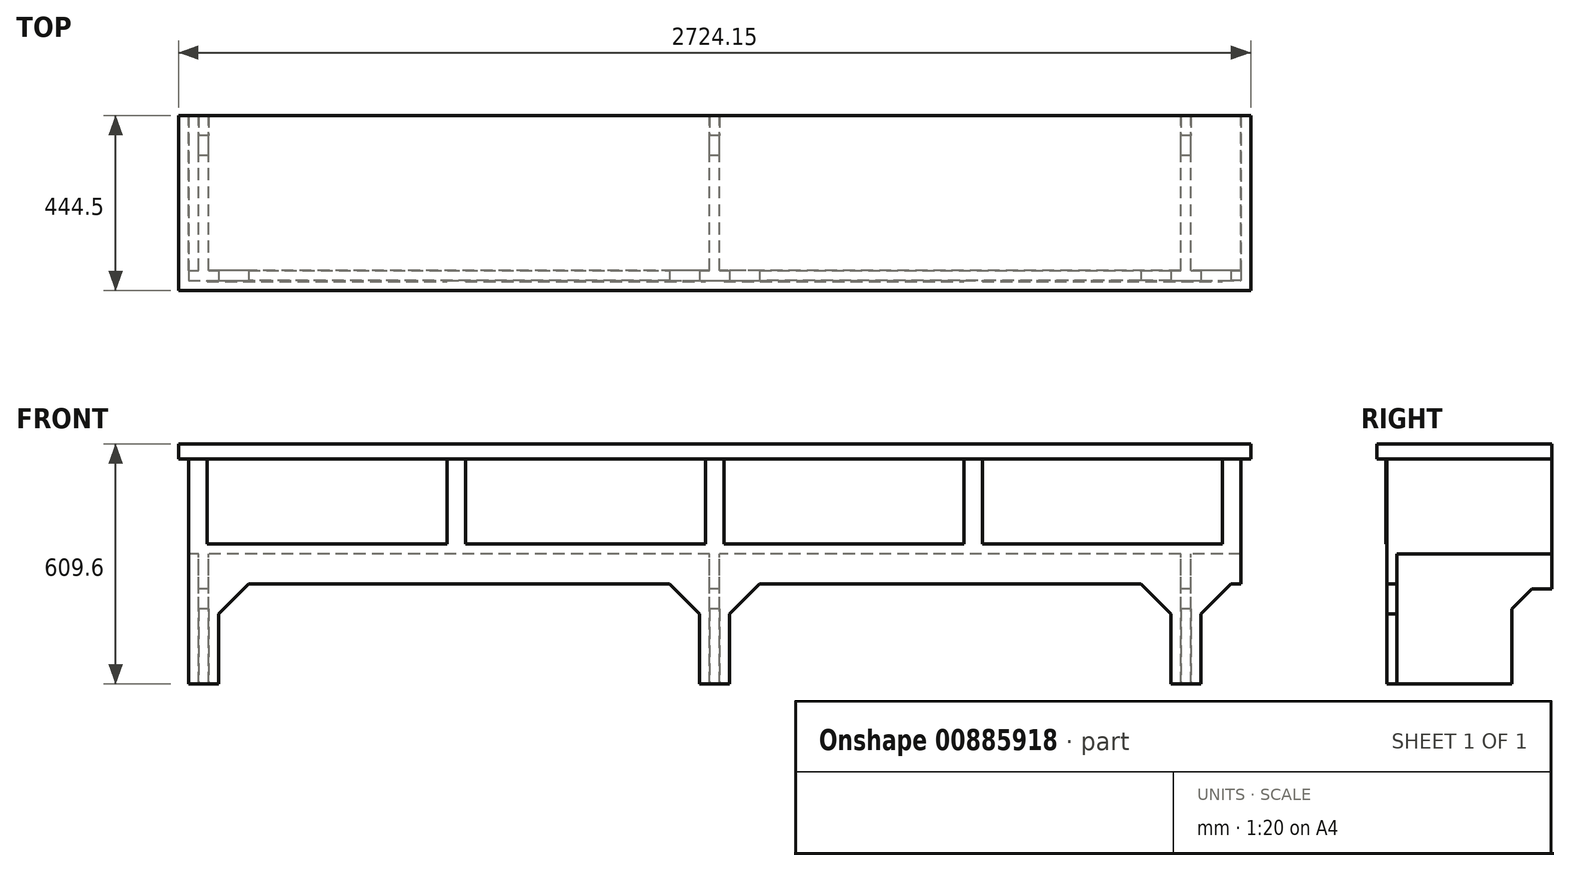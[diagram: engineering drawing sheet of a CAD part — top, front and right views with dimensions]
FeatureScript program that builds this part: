
annotation { "Feature Type Name" : "Feature", "Feature Type Description" : "" }
export const myFeature = defineFeature(function(context is Context, id is Id, definition is map)
    precondition{}
    {
        {
            var Q0;
            Q0=qCreatedBy(makeId("Top.planeOp"),FACE);
            var sketch = newSketch(context, id + "F0", { "sketchPlane" : qUnion([Q0])});
            skLineSegment(sketch, "E0.bottom", {"start": v(-1362.07, 0) * mm, "end": v(1362.07, 0) * mm});
            skLineSegment(sketch, "E0.top", {"start": v(-1362.07, -419.1) * mm, "end": v(1362.07, -419.1) * mm});
            skLineSegment(sketch, "E0.left", {"start": v(-1362.07, 0) * mm, "end": v(-1362.07, -419.1) * mm});
            skLineSegment(sketch, "E0.right", {"start": v(1362.08, 0) * mm, "end": v(1362.08, -419.1) * mm});
            skSolve(sketch);
        }
        {
            var Q0;
            Q0=makeQuery(id+"F0.imprint","IMPRINT",FACE,{"disambiguationData":[TD([[makeQuery(id+"F0.imprint","IMPRINT",EDGE,{"derivedFrom":sQuery(id+"F0.wireOp",EDGE,"E0.bottom")}),-1.0]])]});
            extrude(context, id + "F1", {"entities" : qUnion([Q0]), "oppositeDirection" : true, "depth" : 609.6 * mm, "offsetDistance" : 25.4 * mm});
        }
        {
            var Q0;
            Q0=qCreatedBy(makeId("Right.planeOp"),FACE);
            var sketch = newSketch(context, id + "F2", { "sketchPlane" : qUnion([Q0])});
            skLineSegment(sketch, "E1", {"start": v(-101.6, -609.6) * mm, "end": v(-101.6, -419.1) * mm});
            skLineSegment(sketch, "E2", {"start": v(-50.8, -368.3) * mm, "end": v(-101.6, -419.1) * mm});
            skLineSegment(sketch, "E3", {"start": v(-50.8, -368.3) * mm, "end": v(0, -368.3) * mm});
            skLineSegment(sketch, "E4", {"start": v(0, -368.3) * mm, "end": v(0, -609.6) * mm});
            skLineSegment(sketch, "E5", {"start": v(0, -609.6) * mm, "end": v(-101.6, -609.6) * mm});
            skSolve(sketch);
        }
        {
            var Q0;
            Q0=qSketchRegion(id+"F2",true);
            extrude(context, id + "F3", {"entities" : qUnion([Q0]), "operationType" : NewBodyOperationType.REMOVE, "endBound" : BoundingType.THROUGH_ALL, "depth" : 25.4 * mm, "offsetDistance" : 25.4 * mm, "hasSecondDirection" : true, "secondDirectionBound" : SecondDirectionBoundingType.THROUGH_ALL, "secondDirectionOppositeDirection" : true, "secondDirectionDepth" : 25.4 * mm});
        }
        {
            var Q0;
            Q0=makeQuery(id+"F1.opExtrude","SWEPT_FACE",FACE,{"disambiguationData":[OSD([sQuery(id+"F0.wireOp",EDGE,"E0.top")])]});
            var sketch = newSketch(context, id + "F4", { "sketchPlane" : qUnion([Q0])});
            skLineSegment(sketch, "E6.bottom", {"start": v(1362.08, -38.1) * mm, "end": v(1336.68, -38.1) * mm});
            skLineSegment(sketch, "E6.top", {"start": v(1362.08, -609.6) * mm, "end": v(1336.68, -609.6) * mm});
            skLineSegment(sketch, "E6.left", {"start": v(1362.08, -38.1) * mm, "end": v(1362.08, -609.6) * mm});
            skLineSegment(sketch, "E6.right", {"start": v(1336.68, -38.1) * mm, "end": v(1336.68, -609.6) * mm});
            skLineSegment(sketch, "E7.bottom", {"start": v(-1362.07, -38.1) * mm, "end": v(-1336.67, -38.1) * mm});
            skLineSegment(sketch, "E7.top", {"start": v(-1362.07, -609.6) * mm, "end": v(-1336.67, -609.6) * mm});
            skLineSegment(sketch, "E7.left", {"start": v(-1362.07, -38.1) * mm, "end": v(-1362.07, -609.6) * mm});
            skLineSegment(sketch, "E7.right", {"start": v(-1336.67, -38.1) * mm, "end": v(-1336.67, -609.6) * mm});
            skSolve(sketch);
        }
        {
            var Q0;
            Q0=qSketchRegion(id+"F4",true);
            extrude(context, id + "F5", {"entities" : qUnion([Q0]), "operationType" : NewBodyOperationType.REMOVE, "endBound" : BoundingType.THROUGH_ALL, "oppositeDirection" : true, "depth" : 25.4 * mm, "offsetDistance" : 25.4 * mm});
        }
        {
            var Q0;
            Q0=makeQuery(id+"F1.opExtrude","SWEPT_FACE",FACE,{"disambiguationData":[OSD([sQuery(id+"F0.wireOp",EDGE,"E0.top")])]});
            var sketch = newSketch(context, id + "F6", { "sketchPlane" : qUnion([Q0])});
            skLineSegment(sketch, "E8.bottom", {"start": v(-1260.47, -609.6) * mm, "end": v(-38.1, -609.6) * mm});
            skLineSegment(sketch, "E8.left", {"start": v(-1260.47, -609.6) * mm, "end": v(-1260.47, -431.8) * mm});
            skLineSegment(sketch, "E8.right", {"start": v(-38.1, -609.6) * mm, "end": v(-38.1, -431.8) * mm});
            skLineSegment(sketch, "E9.bottom", {"start": v(38.1, -609.6) * mm, "end": v(1158.88, -609.6) * mm});
            skLineSegment(sketch, "E9.left", {"start": v(38.1, -609.6) * mm, "end": v(38.1, -431.8) * mm});
            skLineSegment(sketch, "E9.right", {"start": v(1158.88, -609.6) * mm, "end": v(1158.88, -431.8) * mm});
            skLineSegment(sketch, "E10", {"start": v(-38.1, 0) * mm, "end": v(38.1, 0) * mm, "construction": true});
            skLineSegment(sketch, "E11", {"start": v(-1260.47, -609.6) * mm, "end": v(-1336.67, -609.6) * mm, "construction": true});
            skLineSegment(sketch, "E12", {"start": v(1158.88, -609.6) * mm, "end": v(1235.08, -609.6) * mm, "construction": true});
            skLineSegment(sketch, "E13", {"start": v(1082.68, -355.6) * mm, "end": v(114.3, -355.6) * mm});
            skLineSegment(sketch, "E14", {"start": v(-114.3, -355.6) * mm, "end": v(-1184.28, -355.6) * mm});
            skLineSegment(sketch, "E15", {"start": v(-1260.48, -431.8) * mm, "end": v(-1184.28, -355.6) * mm});
            skLineSegment(sketch, "E16", {"start": v(-114.3, -355.6) * mm, "end": v(-38.1, -431.8) * mm});
            skLineSegment(sketch, "E17", {"start": v(38.1, -431.8) * mm, "end": v(114.3, -355.6) * mm});
            skLineSegment(sketch, "E18", {"start": v(1158.88, -431.8) * mm, "end": v(1082.68, -355.6) * mm});
            skLineSegment(sketch, "E19", {"start": v(-649.29, -355.6) * mm, "end": v(-649.29, -609.6) * mm, "construction": true});
            skLineSegment(sketch, "E20", {"start": v(598.49, -355.6) * mm, "end": v(598.49, -609.6) * mm, "construction": true});
            skLineSegment(sketch, "E21", {"start": v(1235.08, -609.6) * mm, "end": v(1235.08, -431.8) * mm});
            skLineSegment(sketch, "E22", {"start": v(1235.08, -431.8) * mm, "end": v(1311.28, -355.6) * mm});
            skLineSegment(sketch, "E23", {"start": v(1336.68, -355.6) * mm, "end": v(1336.68, -609.6) * mm});
            skLineSegment(sketch, "E24", {"start": v(1336.68, -609.6) * mm, "end": v(1235.08, -609.6) * mm});
            skLineSegment(sketch, "E25", {"start": v(1336.68, -355.6) * mm, "end": v(1311.28, -355.6) * mm});
            skSolve(sketch);
        }
        {
            var Q0;
            Q0=qSketchRegion(id+"F6",true);
            extrude(context, id + "F7", {"entities" : qUnion([Q0]), "operationType" : NewBodyOperationType.REMOVE, "endBound" : BoundingType.THROUGH_ALL, "oppositeDirection" : true, "depth" : 25.4 * mm, "offsetDistance" : 25.4 * mm});
        }
        {
            var Q0;
            Q0=makeQuery(id+"F1.opExtrude","SWEPT_FACE",FACE,{"disambiguationData":[OSD([sQuery(id+"F0.wireOp",EDGE,"E0.top")])]});
            var sketch = newSketch(context, id + "F8", { "sketchPlane" : qUnion([Q0])});
            skLineSegment(sketch, "E26.bottom", {"start": v(-1289.68, -38.1) * mm, "end": v(-680.09, -38.1) * mm});
            skLineSegment(sketch, "E26.top", {"start": v(-1289.68, -254) * mm, "end": v(-680.09, -254) * mm});
            skLineSegment(sketch, "E26.left", {"start": v(-1289.68, -38.1) * mm, "end": v(-1289.68, -254) * mm});
            skLineSegment(sketch, "E26.right", {"start": v(-680.09, -38.1) * mm, "end": v(-680.09, -254) * mm});
            skLineSegment(sketch, "E27.bottom", {"start": v(-633.1, -38.1) * mm, "end": v(-23.5, -38.1) * mm});
            skLineSegment(sketch, "E27.top", {"start": v(-633.1, -254) * mm, "end": v(-23.5, -254) * mm});
            skLineSegment(sketch, "E27.left", {"start": v(-633.1, -38.1) * mm, "end": v(-633.1, -254) * mm});
            skLineSegment(sketch, "E27.right", {"start": v(-23.5, -38.1) * mm, "end": v(-23.5, -254) * mm});
            skLineSegment(sketch, "E28.bottom", {"start": v(23.5, -38.1) * mm, "end": v(633.1, -38.1) * mm});
            skLineSegment(sketch, "E28.top", {"start": v(23.5, -254) * mm, "end": v(633.1, -254) * mm});
            skLineSegment(sketch, "E28.left", {"start": v(23.5, -38.1) * mm, "end": v(23.5, -254) * mm});
            skLineSegment(sketch, "E28.right", {"start": v(633.1, -38.1) * mm, "end": v(633.1, -254) * mm});
            skLineSegment(sketch, "E29.bottom", {"start": v(680.09, -38.1) * mm, "end": v(1289.68, -38.1) * mm});
            skLineSegment(sketch, "E29.top", {"start": v(680.09, -254) * mm, "end": v(1289.68, -254) * mm});
            skLineSegment(sketch, "E29.left", {"start": v(680.09, -38.1) * mm, "end": v(680.09, -254) * mm});
            skLineSegment(sketch, "E29.right", {"start": v(1289.68, -38.1) * mm, "end": v(1289.68, -254) * mm});
            skLineSegment(sketch, "E30", {"start": v(-1336.67, -254) * mm, "end": v(-1289.68, -254) * mm, "construction": true});
            skLineSegment(sketch, "E31", {"start": v(-680.09, -254) * mm, "end": v(-633.1, -254) * mm, "construction": true});
            skLineSegment(sketch, "E32", {"start": v(-23.5, -254) * mm, "end": v(23.5, -254) * mm, "construction": true});
            skLineSegment(sketch, "E33", {"start": v(633.1, -254) * mm, "end": v(680.09, -254) * mm, "construction": true});
            skLineSegment(sketch, "E34", {"start": v(0, 0) * mm, "end": v(0, -254) * mm, "construction": true});
            skSolve(sketch);
        }
        {
            var Q0;
            Q0=qSketchRegion(id+"F8",true);
            extrude(context, id + "F9", {"entities" : qUnion([Q0]), "operationType" : NewBodyOperationType.ADD, "depth" : 2.54 * mm, "offsetDistance" : 25.4 * mm});
        }
        {
            var Q0;
            Q0=makeQuery(id+"F1.opExtrude","SWEPT_FACE",FACE,{"disambiguationData":[OSD([sQuery(id+"F0.wireOp",EDGE,"E0.bottom")])]});
            var sketch = newSketch(context, id + "F10", { "sketchPlane" : qUnion([Q0])});
            skLineSegment(sketch, "E35.bottom", {"start": v(-1209.68, -609.6) * mm, "end": v(-1184.28, -609.6) * mm});
            skLineSegment(sketch, "E35.left", {"start": v(-1209.68, -609.6) * mm, "end": v(-1209.68, -279.4) * mm});
            skLineSegment(sketch, "E35.right", {"start": v(-1184.28, -609.6) * mm, "end": v(-1184.28, -279.4) * mm});
            skLineSegment(sketch, "E36.bottom", {"start": v(-12.7, -609.6) * mm, "end": v(12.7, -609.6) * mm});
            skLineSegment(sketch, "E36.left", {"start": v(-12.7, -609.6) * mm, "end": v(-12.7, -279.4) * mm});
            skLineSegment(sketch, "E36.right", {"start": v(12.7, -609.6) * mm, "end": v(12.7, -279.4) * mm});
            skLineSegment(sketch, "E37.bottom", {"start": v(1285.88, -609.6) * mm, "end": v(1311.28, -609.6) * mm});
            skLineSegment(sketch, "E37.left", {"start": v(1285.88, -609.6) * mm, "end": v(1285.88, -279.4) * mm});
            skLineSegment(sketch, "E37.right", {"start": v(1311.28, -609.6) * mm, "end": v(1311.28, -279.4) * mm});
            skLineSegment(sketch, "E38", {"start": v(-1336.68, -279.4) * mm, "end": v(-1209.68, -279.4) * mm});
            skLineSegment(sketch, "E39.trimOffspring", {"start": v(-1184.28, -279.4) * mm, "end": v(-12.7, -279.4) * mm});
            skLineSegment(sketch, "E40.trimOffspring", {"start": v(12.7, -279.4) * mm, "end": v(1285.88, -279.4) * mm});
            skLineSegment(sketch, "E41.trimOffspring", {"start": v(1311.28, -279.4) * mm, "end": v(1336.67, -279.4) * mm});
            skLineSegment(sketch, "E42", {"start": v(-1336.68, -279.4) * mm, "end": v(-1336.68, -635) * mm});
            skLineSegment(sketch, "E43", {"start": v(-1336.68, -635) * mm, "end": v(1336.67, -635) * mm});
            skLineSegment(sketch, "E44", {"start": v(1336.67, -635) * mm, "end": v(1336.67, -279.4) * mm});
            skSolve(sketch);
        }
        {
            var Q0;
            Q0=qSketchRegion(id+"F10",true);
            var Q1;
            Q1=makeQuery(id+"F1.opExtrude","SWEPT_FACE",FACE,{"disambiguationData":[OSD([sQuery(id+"F0.wireOp",EDGE,"E0.top")])]});
            extrude(context, id + "F11", {"entities" : qUnion([Q0]), "operationType" : NewBodyOperationType.REMOVE, "endBound" : BoundingType.UP_TO_SURFACE, "oppositeDirection" : true, "depth" : 25.4 * mm, "endBoundEntityFace" : qUnion([Q1]), "hasOffset" : true, "offsetDistance" : 25.4 * mm});
        }
        {
            var Q0;
            Q0=makeQuery(id+"F1.opExtrude","SWEPT_FACE",FACE,{"disambiguationData":[OSD([sQuery(id+"F0.wireOp",EDGE,"E0.top")])]});
            var sketch = newSketch(context, id + "F12", { "sketchPlane" : qUnion([Q0])});
            skLineSegment(sketch, "E45.bottom", {"start": v(-1362.07, 0) * mm, "end": v(1362.08, 0) * mm});
            skLineSegment(sketch, "E45.top", {"start": v(-1362.07, -38.1) * mm, "end": v(1362.08, -38.1) * mm});
            skLineSegment(sketch, "E45.left", {"start": v(-1362.07, 0) * mm, "end": v(-1362.07, -38.1) * mm});
            skLineSegment(sketch, "E45.right", {"start": v(1362.08, 0) * mm, "end": v(1362.08, -38.1) * mm});
            skSolve(sketch);
        }
        {
            var Q0;
            Q0=qSketchRegion(id+"F12",true);
            extrude(context, id + "F13", {"entities" : qUnion([Q0]), "operationType" : NewBodyOperationType.ADD, "depth" : 25.4 * mm, "offsetDistance" : 25.4 * mm});
        }
    });
